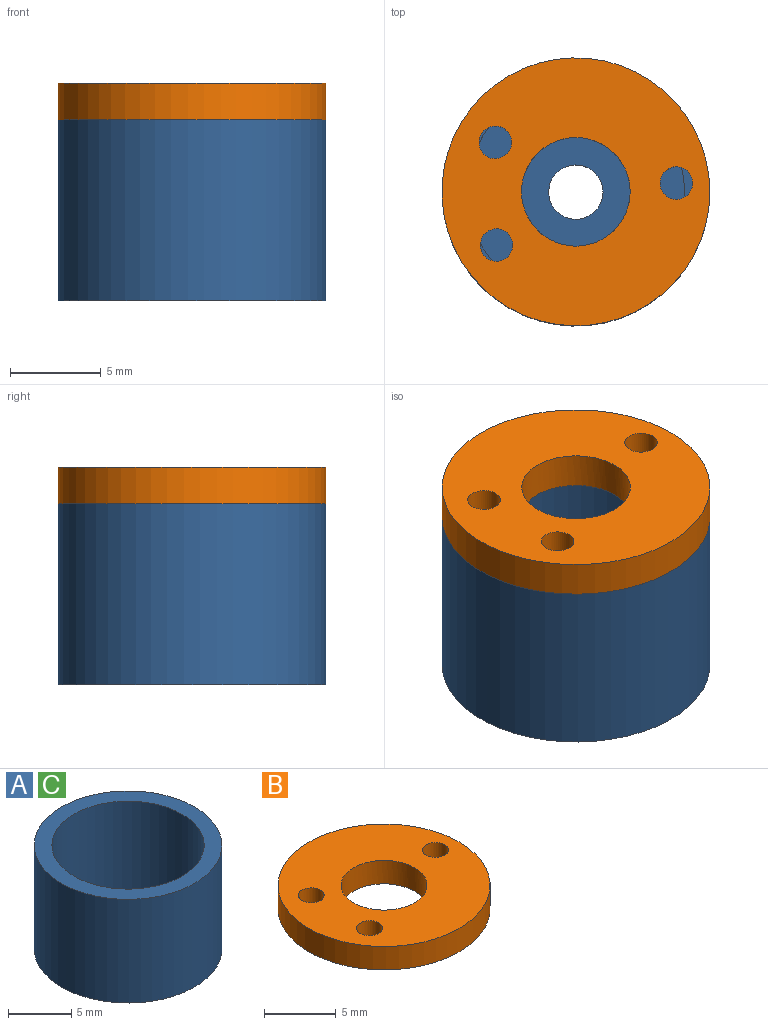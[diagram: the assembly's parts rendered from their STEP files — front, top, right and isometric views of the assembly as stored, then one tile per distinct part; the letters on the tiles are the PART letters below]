
ASSEMBLY  parts=3 mates=1
PART A: 6 faces, bbox 14.8x14.8x10 mm
  f0: cylinder r=7.4mm len=14.8mm, axis (0,0,1), area 464.8mm2, adj f1,f2
  f1: plane 14.8x14.8mm, normal (0,0,-1), area 164.9mm2, adj f0,f3
  f2: plane 14.8x14.8mm, normal (0,0,1), area 58.9mm2, adj f0,f5
  f3: cylinder r=1.5mm len=3mm, axis (0,0,1), area 14.1mm2, adj f1,f4
  f4: plane 12x12mm, normal (0,0,1), area 106mm2, adj f3,f5
  f5: cylinder r=6mm len=12mm, axis (0,0,1), area 320.4mm2, adj f2,f4
PART B: 7 faces, bbox 14.8x14.8x2 mm
  f0: cylinder r=7.4mm len=14.8mm, axis (0,0,-1), area 93mm2, adj f1,f2
  f1: plane 14.8x14.8mm, normal (0,0,1), area 136.1mm2, adj f0,f3,f4,f5,f6
  f2: plane 14.8x14.8mm, normal (0,0,-1), area 136.1mm2, adj f0,f3,f4,f5,f6
  f3: cylinder r=3mm len=6mm, axis (0,0,-1), area 37.7mm2, adj f1,f2
  f4: cylinder r=0.9mm len=2mm, axis (0,0,1), area 11.3mm2, adj f1,f2
  f5: cylinder r=0.9mm len=2mm, axis (0,0,1), area 11.3mm2, adj f1,f2
  f6: cylinder r=0.9mm len=2mm, axis (0,0,1), area 11.3mm2, adj f1,f2
PART C: same geometry as A
PLACE A t=(29.11,-38.98,-1.16)mm
PLACE B t=(-16.47,26.62,-1.16)mm
PLACE C t=(29.11,-38.98,-1.16)mm
MATE fastened B.f0 <-> C.f0  axis (0,0,-1) through (-83,-25.22,-1.16)mm
